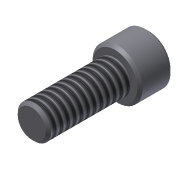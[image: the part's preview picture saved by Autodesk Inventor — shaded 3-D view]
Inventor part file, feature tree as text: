
AUTODESK INVENTOR PART (.ipt)
format: ipt  version: 2011 (Build 150239000, 239)  size: 110,592 bytes
history: native  units: in
note: dims shown in document units (in); Inventor stores cm internally (conversion verified against a paired STEP export)
features: extrude x3, sketch x3, chamfer x1, thread x1
ambient origin geometry x8: Origin, YZ Plane, XZ Plane, XY Plane, X Axis, Y Axis, Z Axis, Center Point
bodies: Solid1 (feature_tree)
feature tree (8):
  extrude  "Extrusion1"  Depth=0.625in TaperAngle=0.0deg
  extrude  "Extrusion2"  Depth=0.25in TaperAngle=0.0deg
  extrude  "Extrusion3"  Depth=0.125in TaperAngle=0.0deg
  chamfer  "Chamfer1"  Distance=0.02in Angle=45.0deg
  thread  "Thread1"  [1 undecoded]
  sketch  "Sketch1"  dims[d0=0.25in d1=0.625in d2=0.0in]
  sketch  "Sketch2"  dims[d3=0.375in d4=0.25in d5=0.0in]
  sketch  "Sketch3"  dims[d6=0.1875in d7=0.125in d8=0.0in d9=0.02in d10=0.125in d11=45.0deg d12=1.0in d13=0.0in]
note: 1 required parameter value undecoded (feature->parameter linkage not recoverable at this tier; creation-order binding heuristic only, values carry confidence <= 0.55)
